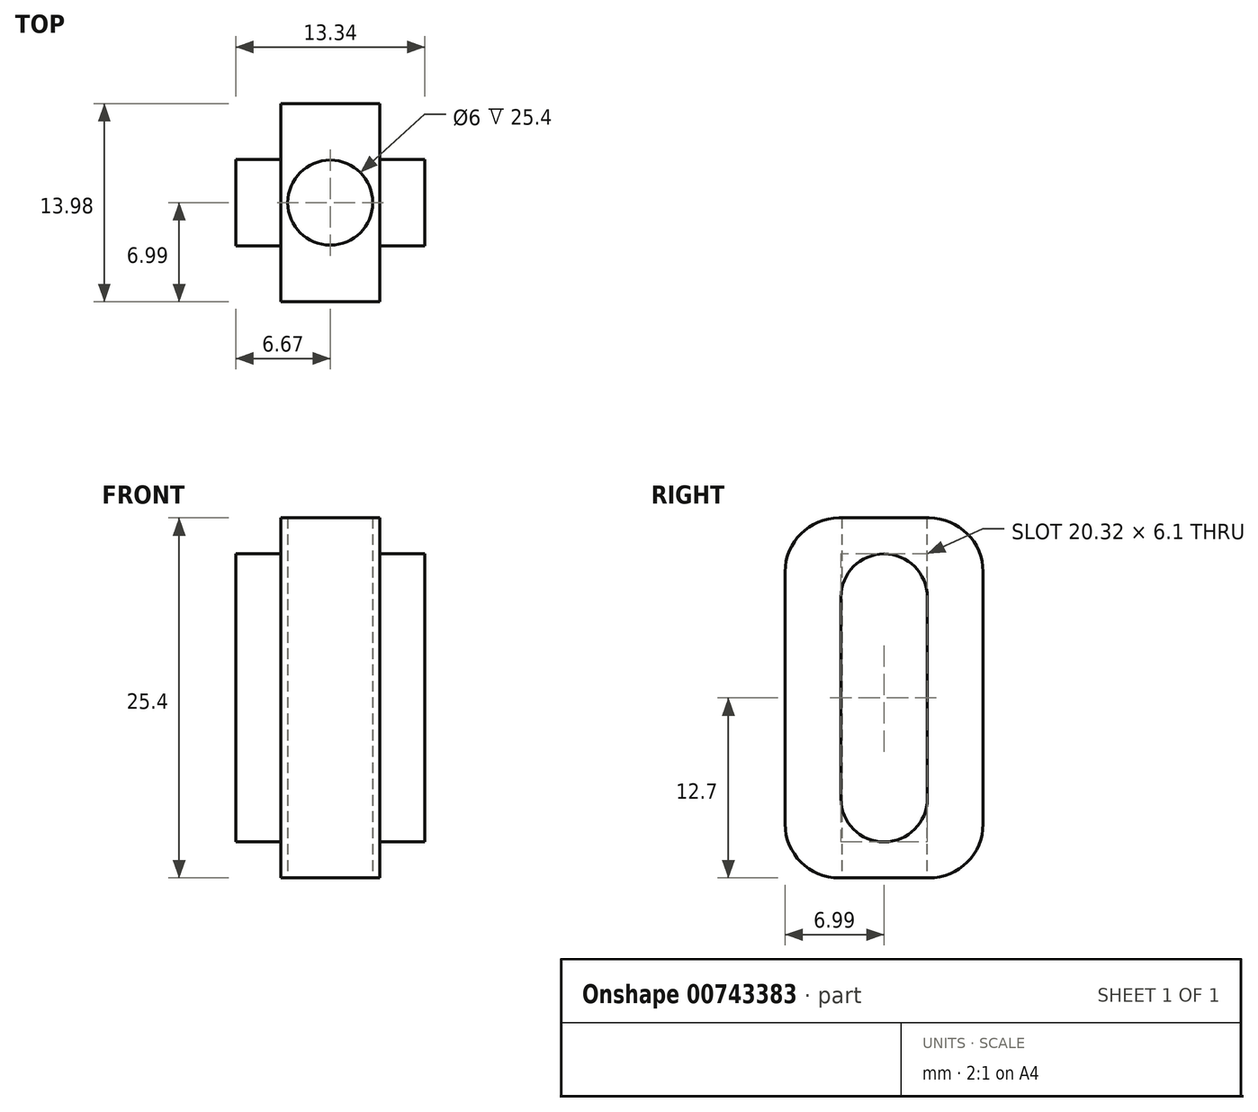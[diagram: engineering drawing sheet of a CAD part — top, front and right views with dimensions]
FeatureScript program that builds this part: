
annotation { "Feature Type Name" : "Feature", "Feature Type Description" : "" }
export const myFeature = defineFeature(function(context is Context, id is Id, definition is map)
    precondition{}
    {
        {
            var Q0;
            Q0=qCreatedBy(makeId("Top.planeOp"),FACE);
            var sketch = newSketch(context, id + "F0", { "sketchPlane" : qUnion([Q0])});
            skLineSegment(sketch, "E0.bottom", {"start": v(3.5, -6.99) * mm, "end": v(-3.5, -6.99) * mm});
            skLineSegment(sketch, "E0.top", {"start": v(3.5, 6.99) * mm, "end": v(-3.5, 6.99) * mm});
            skLineSegment(sketch, "E0.left", {"start": v(3.5, -6.99) * mm, "end": v(3.5, 6.99) * mm});
            skLineSegment(sketch, "E0.right", {"start": v(-3.5, -6.99) * mm, "end": v(-3.5, 6.99) * mm});
            skPoint(sketch, "E0.middle", {"position": v(0, 0) * mm});
            skSolve(sketch);
        }
        {
            var Q0;
            Q0 = qSketchRegion(id + "F0", true);
            extrude(context, id + "F1", {"entities" : qUnion([Q0]), "depth" : 25.4 * mm, "offsetDistance" : 25.4 * mm});
        }
        {
            var Q0;
            Q0=makeQuery(id+"F1.opExtrude","CAP_FACE",FACE,{"disambiguationData":[OSD([sQuery(id+"F0.wireOp",EDGE,"E0.bottom"),sQuery(id+"F0.wireOp",EDGE,"E0.top"),sQuery(id+"F0.wireOp",EDGE,"E0.left"),sQuery(id+"F0.wireOp",EDGE,"E0.right")])],"isStart":true});
            var sketch = newSketch(context, id + "F2", { "sketchPlane" : qUnion([Q0])});
            skCircle(sketch, "E1", {"center": v(0, 0) * mm, "radius": 3 * mm});
            skSolve(sketch);
        }
        {
            var Q0;
            Q0 = qSketchRegion(id + "F2", true);
            extrude(context, id + "F3", {"entities" : qUnion([Q0]), "operationType" : NewBodyOperationType.REMOVE, "oppositeDirection" : true, "depth" : 25.4 * mm, "offsetDistance" : 25.4 * mm});
        }
        {
            var Q0;
            Q0=makeQuery(id+"F1.opExtrude","SWEPT_FACE",FACE,{"disambiguationData":[OSD([sQuery(id+"F0.wireOp",EDGE,"E0.left")])]});
            var sketch = newSketch(context, id + "F4", { "sketchPlane" : qUnion([Q0])});
            skLineSegment(sketch, "E2", {"start": v(0, 25.4) * mm, "end": v(0, 0) * mm});
            skLineSegment(sketch, "E3.bottom", {"start": v(3.05, 2.54) * mm, "end": v(-3.05, 2.54) * mm});
            skLineSegment(sketch, "E3.top", {"start": v(3.05, 22.86) * mm, "end": v(-3.05, 22.86) * mm});
            skLineSegment(sketch, "E3.left", {"start": v(3.05, 2.54) * mm, "end": v(3.05, 22.86) * mm});
            skLineSegment(sketch, "E3.right", {"start": v(-3.05, 2.54) * mm, "end": v(-3.05, 22.86) * mm});
            skPoint(sketch, "E3.middle", {"position": v(0, 12.7) * mm});
            skSolve(sketch);
        }
        {
            var Q0;
            Q0 = qSketchRegion(id + "F4", true);
            extrude(context, id + "F5", {"entities" : qUnion([Q0]), "operationType" : NewBodyOperationType.ADD, "depth" : 3.17 * mm, "offsetDistance" : 25.4 * mm});
        }
        {
            var Q0;
            Q0=makeQuery(id+"F5.opExtrude","SWEPT_EDGE",EDGE,{"disambiguationData":[OSD([sQuery(id+"F4.wireOp",EDGE,"E3.top"),sQuery(id+"F4.wireOp",EDGE,"E3.right")])]});
            var Q1;
            Q1=makeQuery(id+"F5.opExtrude","SWEPT_EDGE",EDGE,{"disambiguationData":[OSD([sQuery(id+"F4.wireOp",EDGE,"E3.top"),sQuery(id+"F4.wireOp",EDGE,"E3.left")])]});
            var Q2;
            Q2=makeQuery(id+"F5.opExtrude","SWEPT_EDGE",EDGE,{"disambiguationData":[OSD([sQuery(id+"F4.wireOp",EDGE,"E3.bottom"),sQuery(id+"F4.wireOp",EDGE,"E3.left")])]});
            var Q3;
            Q3=makeQuery(id+"F5.opExtrude","SWEPT_EDGE",EDGE,{"disambiguationData":[OSD([sQuery(id+"F4.wireOp",EDGE,"E3.bottom"),sQuery(id+"F4.wireOp",EDGE,"E3.right")])]});
            fillet(context, id + "F6", {"entities" : qUnion([Q0, Q1, Q2, Q3]), "radius" : 3.05 * mm, "tangentPropagation" : true, "allowEdgeOverflow" : false});
        }
        {
            var Q0;
            Q0=makeQuery(id+"F1.opExtrude","SWEPT_BODY",BODY,{"disambiguationData":[OSD([sQuery(id+"F0.wireOp",EDGE,"E0.bottom"),sQuery(id+"F0.wireOp",EDGE,"E0.top"),sQuery(id+"F0.wireOp",EDGE,"E0.left"),sQuery(id+"F0.wireOp",EDGE,"E0.right")])]});
            var Q1;
            Q1=qCreatedBy(makeId("Right.planeOp"),FACE);
            mirror(context, id + "F7", {"operationType" : NewBodyOperationType.ADD, "entities" : qUnion([Q0]), "mirrorPlane" : qUnion([Q1])});
        }
        {
            var Q0;
            Q0=makeQuery(id+"F1.opExtrude","CAP_EDGE",EDGE,{"disambiguationData":[OSD([sQuery(id+"F0.wireOp",EDGE,"E0.bottom")])],"isStart":true});
            var Q1;
            Q1=makeQuery(id+"F1.opExtrude","CAP_EDGE",EDGE,{"disambiguationData":[OSD([sQuery(id+"F0.wireOp",EDGE,"E0.top")])],"isStart":true});
            var Q2;
            Q2=makeQuery(id+"F1.opExtrude","CAP_EDGE",EDGE,{"disambiguationData":[OSD([sQuery(id+"F0.wireOp",EDGE,"E0.top")])],"isStart":false});
            var Q3;
            Q3=makeQuery(id+"F1.opExtrude","CAP_EDGE",EDGE,{"disambiguationData":[OSD([sQuery(id+"F0.wireOp",EDGE,"E0.bottom")])],"isStart":false});
            fillet(context, id + "F8", {"entities" : qUnion([Q0, Q1, Q2, Q3]), "radius" : 3.8 * mm, "tangentPropagation" : true, "allowEdgeOverflow" : false});
        }
    });
